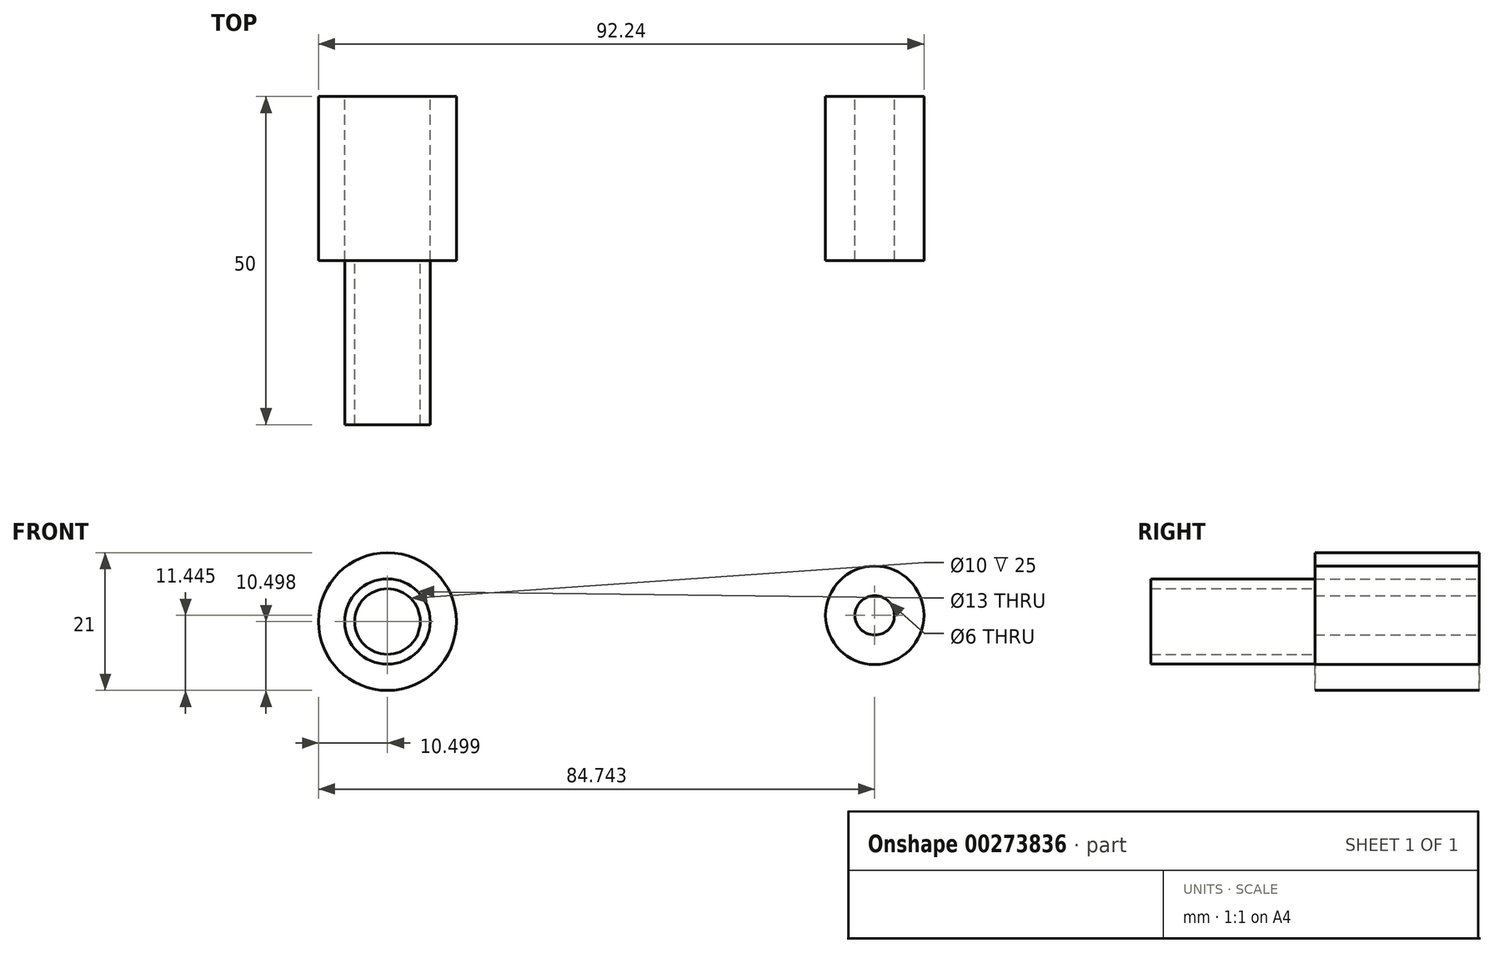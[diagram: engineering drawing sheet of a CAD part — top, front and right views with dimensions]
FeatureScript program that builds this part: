
annotation { "Feature Type Name" : "Feature", "Feature Type Description" : "" }
export const myFeature = defineFeature(function(context is Context, id is Id, definition is map)
    precondition{}
    {
        {
            var Q0;
            Q0=qCreatedBy(makeId("Front.planeOp"),FACE);
            var sketch = newSketch(context, id + "F0", { "sketchPlane" : qUnion([Q0])});
            skCircle(sketch, "E0", {"center": v(-8.68, 14.44) * mm, "radius": 10.5 * mm});
            skCircle(sketch, "E1", {"center": v(-8.68, 14.44) * mm, "radius": 6.5 * mm});
            skCircle(sketch, "E2", {"center": v(65.56, 15.38) * mm, "radius": 7.5 * mm});
            skCircle(sketch, "E3", {"center": v(65.56, 15.38) * mm, "radius": 3 * mm});
            skSolve(sketch);
        }
        {
            var Q0;
            Q0=makeQuery(id+"F0.imprint","IMPRINT",FACE,{"disambiguationData":[TD([[makeQuery(id+"F0.imprint","IMPRINT",EDGE,{"derivedFrom":sQuery(id+"F0.wireOp",EDGE,"E0")}),1.0]])]});
            var Q1;
            Q1=makeQuery(id+"F0.imprint","IMPRINT",FACE,{"disambiguationData":[TD([[makeQuery(id+"F0.imprint","IMPRINT",EDGE,{"derivedFrom":sQuery(id+"F0.wireOp",EDGE,"E2")}),1.0]])]});
            extrude(context, id + "F1", {"entities" : qUnion([Q0, Q1]), "depth" : 25 * mm});
        }
        {
            var Q0;
            Q0=makeQuery(id+"F1.opExtrude","CAP_FACE",FACE,{"disambiguationData":[OSD([sQuery(id+"F0.wireOp",EDGE,"E0"),sQuery(id+"F0.wireOp",EDGE,"E1")])],"isStart":false});
            var sketch = newSketch(context, id + "F2", { "sketchPlane" : qUnion([Q0])});
            skCircle(sketch, "E4", {"center": v(-8.68, 14.44) * mm, "radius": 5 * mm});
            skSolve(sketch);
        }
        {
            var Q0;
            Q0=makeQuery(id+"F2.imprint","IMPRINT",FACE,{"disambiguationData":[TD([[makeQuery(id+"F2.imprint","IMPRINT",EDGE,{"derivedFrom":sQuery(id+"F2.wireOp",EDGE,"E4")}),-1.0]])]});
            extrude(context, id + "F3", {"entities" : qUnion([Q0]), "depth" : 25 * mm});
        }
    });
